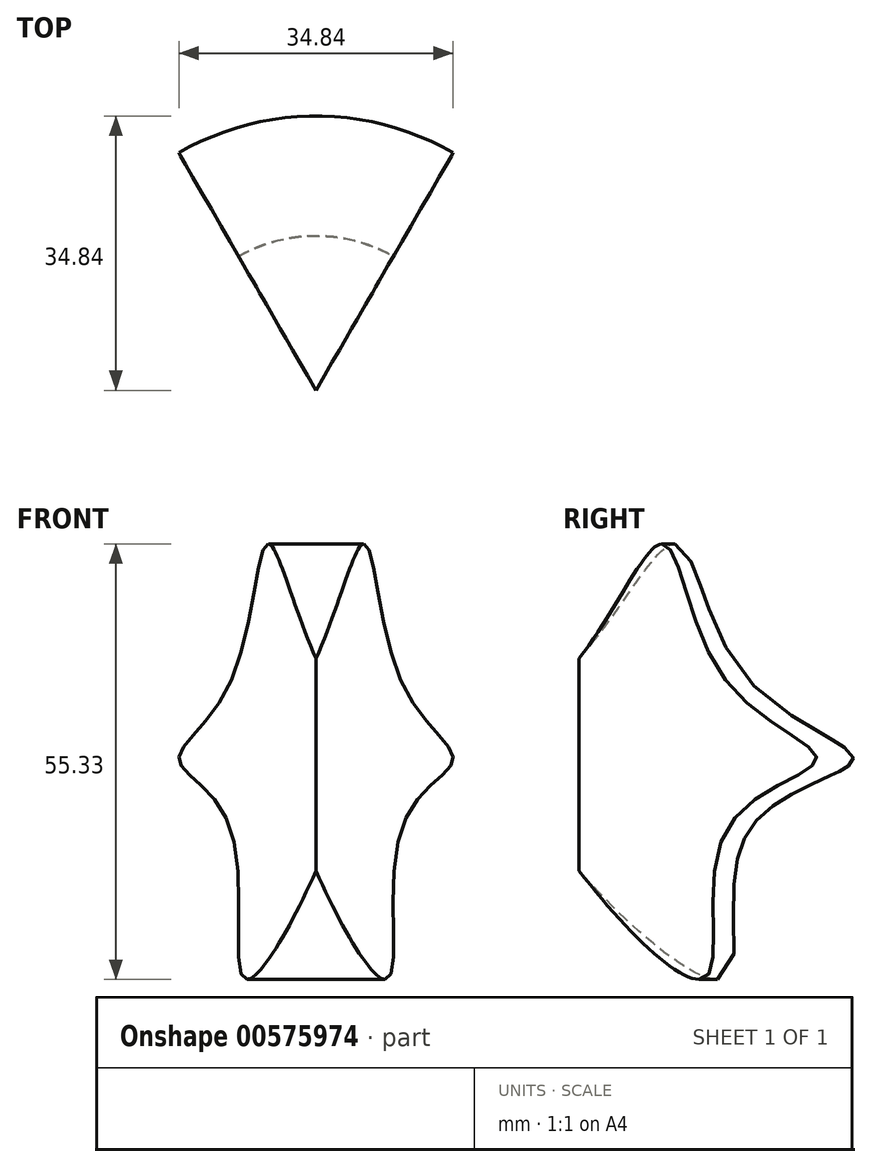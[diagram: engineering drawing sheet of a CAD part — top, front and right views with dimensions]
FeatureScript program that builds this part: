
annotation { "Feature Type Name" : "Feature", "Feature Type Description" : "" }
export const myFeature = defineFeature(function(context is Context, id is Id, definition is map)
    precondition{}
    {
        {
            var Q0;
            Q0=qCreatedBy(makeId("Right.planeOp"),FACE);
            var sketch = newSketch(context, id + "F0", { "sketchPlane" : qUnion([Q0])});
            skLineSegment(sketch, "E0", {"start": v(0, 29.85) * mm, "end": v(0, 2.85) * mm});
            skFitSpline(sketch, "E1", {"points": [v(0, 29.85) * mm, v(12.48, 44.35) * mm, v(21.4, 27.2) * mm, v(34.83, 16.96) * mm, v(21.5, 7.89) * mm, v(18.82, -10.5) * mm, v(0, 2.85) * mm], "startDerivative": vector(104.56, 115.38) * mm, "endDerivative": vector(-113.92, 129.53) * mm});
            skSolve(sketch);
        }
        {
            var Q0;
            Q0=makeQuery(id+"F0.imprint","IMPRINT",FACE,{"disambiguationData":[TD([[makeQuery(id+"F0.imprint","IMPRINT",EDGE,{"derivedFrom":sQuery(id+"F0.wireOp",EDGE,"E0")}),1.0]])]});
            var Q1;
            Q1=sQuery(id+"F0.wireOp",EDGE,"E1");
            var Q2;
            Q2=sQuery(id+"F0.wireOp",EDGE,"E0");
            revolve(context, id + "F1", {"entities" : qUnion([Q0]), "surfaceEntities" : qUnion([Q1]), "axis" : qUnion([Q2]), "revolveType" : RevolveType.TWO_DIRECTIONS, "angle" : 30 * degree, "angleBack" : 330 * degree});
        }
    });
